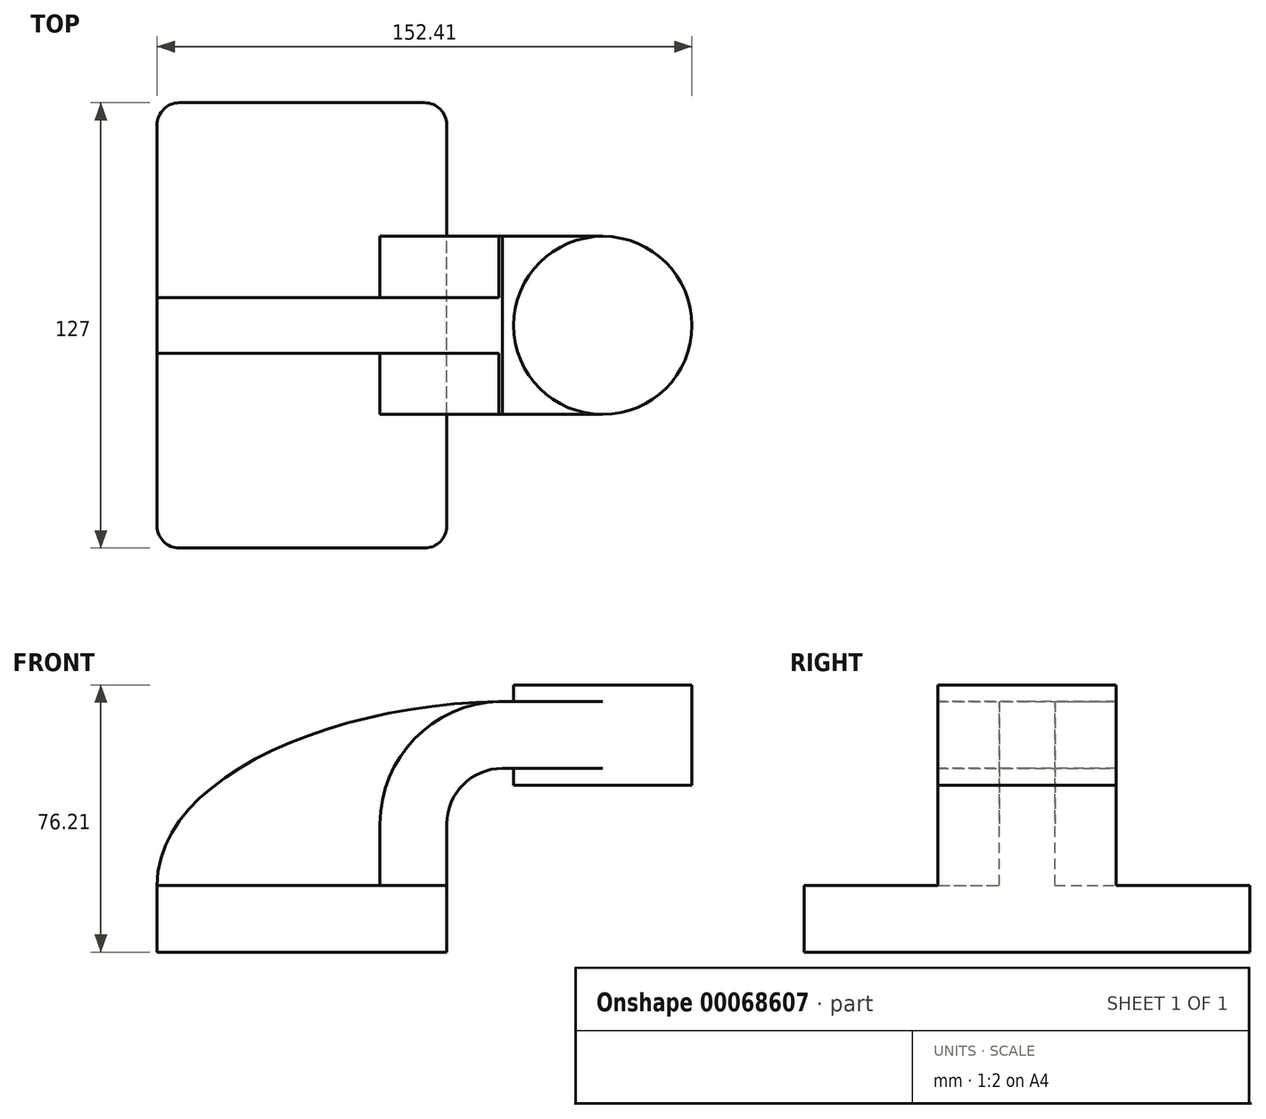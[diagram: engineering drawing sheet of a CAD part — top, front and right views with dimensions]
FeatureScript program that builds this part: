
annotation { "Feature Type Name" : "Feature", "Feature Type Description" : "" }
export const myFeature = defineFeature(function(context is Context, id is Id, definition is map)
    precondition{}
    {
        {
            var Q0;
            Q0=qCreatedBy(makeId("Front.planeOp"),FACE);
            var sketch = newSketch(context, id + "F0", { "sketchPlane" : qUnion([Q0])});
            skLineSegment(sketch, "E0.rect.bottom", {"start": v(-41.28, 9.52) * mm, "end": v(41.27, 9.53) * mm});
            skLineSegment(sketch, "E0.rect.top", {"start": v(-41.28, -9.52) * mm, "end": v(41.28, -9.52) * mm});
            skLineSegment(sketch, "E0.rect.left", {"start": v(-41.28, 9.52) * mm, "end": v(-41.28, -9.53) * mm});
            skLineSegment(sketch, "E0.rect.right", {"start": v(41.27, 9.53) * mm, "end": v(41.28, -9.52) * mm});
            skPoint(sketch, "E0.rect.middle", {"position": v(0, 0) * mm});
            skLineSegment(sketch, "E1.rect.bottom", {"start": v(111.12, 38.1) * mm, "end": v(60.32, 38.1) * mm});
            skLineSegment(sketch, "E1.rect.top", {"start": v(111.12, 66.68) * mm, "end": v(60.32, 66.68) * mm});
            skLineSegment(sketch, "E1.rect.left", {"start": v(111.12, 38.1) * mm, "end": v(111.12, 66.68) * mm});
            skLineSegment(sketch, "E1.rect.right", {"start": v(60.32, 38.1) * mm, "end": v(60.32, 66.68) * mm});
            skPoint(sketch, "E1.rect.middle", {"position": v(85.72, 52.39) * mm});
            skLineSegment(sketch, "E2", {"start": v(41.27, 9.53) * mm, "end": v(41.27, 27) * mm});
            skArc(sketch, "E3", {"start": v(41.27, 27) * mm, "mid": v(45.92, 38.23) * mm, "end": v(57.15, 42.88) * mm});
            skLineSegment(sketch, "E4", {"start": v(57.15, 42.88) * mm, "end": v(85.72, 42.88) * mm});
            skLineSegment(sketch, "E5.0", {"start": v(57.15, 61.93) * mm, "end": v(85.72, 61.93) * mm});
            skArc(sketch, "E5.1", {"start": v(22.22, 27) * mm, "mid": v(32.45, 51.7) * mm, "end": v(57.15, 61.93) * mm});
            skLineSegment(sketch, "E5.2", {"start": v(22.22, 9.53) * mm, "end": v(22.22, 27) * mm});
            skLineSegment(sketch, "E6", {"start": v(85.72, 38.1) * mm, "end": v(85.72, 66.68) * mm});
            skFitSpline(sketch, "E7", {"points": [v(-41.28, 9.52) * mm, v(57.15, 61.93) * mm], "startDerivative": vector(-0.17, 91.25) * mm, "endDerivative": vector(148.08, 1.73) * mm});
            skPoint(sketch, "E8.1.internal.snap0", {"position": v(32.45, 51.7) * mm});
            skSolve(sketch);
        }
        {
            var Q0;
            Q0=makeQuery(id+"F0.imprint","IMPRINT",FACE,{"disambiguationData":[TD([[makeQuery(id+"F0.imprint","IMPRINT",EDGE,{"derivedFrom":sQuery(id+"F0.wireOp",EDGE,"E0.rect.top")}),1.0]])]});
            extrude(context, id + "F1", {"entities" : qUnion([Q0]), "endBound" : BoundingType.SYMMETRIC, "depth" : 127 * mm});
        }
        {
            var Q0;
            {var subQ1=sQuery(id+"F0.wireOp",EDGE,"E2");Q0=makeQuery(id+"F0.imprint","IMPRINT",FACE,{"disambiguationData":[TD([[makeQuery(id+"F0.imprint","IMPRINT",EDGE,{"derivedFrom":subQ1}),1.0]])]});}
            var Q1;
            {var subQ0=sQuery(id+"F0.wireOp",EDGE,"E4");var subQ1=sQuery(id+"F0.wireOp",EDGE,"E1.rect.right");var subQ2=makeQuery(id+"F0.imprint","INTERSECT",VERTEX,{"derivedFrom":[subQ1,subQ0]});Q1=makeQuery(id+"F0.imprint","IMPRINT",FACE,{"disambiguationData":[TD([[makeQuery(id+"F0.imprint","IMPRINT",EDGE,{"disambiguationData":[TD([[subQ2,-1.0]])],"derivedFrom":subQ1}),-1.0]])]});}
            extrude(context, id + "F2", {"entities" : qUnion([Q0, Q1]), "operationType" : NewBodyOperationType.ADD, "endBound" : BoundingType.SYMMETRIC, "depth" : 50.8 * mm});
        }
        {
            var Q0;
            {var subQ3=sQuery(id+"F0.wireOp",EDGE,"E5.2");Q0=makeQuery(id+"F0.imprint","IMPRINT",FACE,{"disambiguationData":[TD([[makeQuery(id+"F0.imprint","IMPRINT",EDGE,{"derivedFrom":subQ3}),1.0]])]});}
            extrude(context, id + "F3", {"entities" : qUnion([Q0]), "operationType" : NewBodyOperationType.ADD, "endBound" : BoundingType.SYMMETRIC, "depth" : 15.88 * mm});
        }
        {
            var Q0;
            {var subQ0=sQuery(id+"F0.wireOp",EDGE,"E1.rect.left");Q0=makeQuery(id+"F0.imprint","IMPRINT",FACE,{"disambiguationData":[TD([[makeQuery(id+"F0.imprint","IMPRINT",EDGE,{"derivedFrom":subQ0}),1.0]])]});}
            var Q1;
            Q1=sQuery(id+"F0.wireOp",EDGE,"E6");
            revolve(context, id + "F4", {"operationType" : NewBodyOperationType.ADD, "entities" : qUnion([Q0]), "axis" : qUnion([Q1]), "revolveType" : RevolveType.FULL});
        }
        {
            var Q0;
            Q0=makeQuery(id+"F1.opExtrude","CAP_EDGE",EDGE,{"disambiguationData":[OSD([sQuery(id+"F0.wireOp",EDGE,"E0.rect.left")])],"isStart":false});
            var Q1;
            Q1=makeQuery(id+"F1.opExtrude","CAP_EDGE",EDGE,{"disambiguationData":[OSD([sQuery(id+"F0.wireOp",EDGE,"E0.rect.right")])],"isStart":false});
            var Q2;
            Q2=makeQuery(id+"F1.opExtrude","CAP_EDGE",EDGE,{"disambiguationData":[OSD([sQuery(id+"F0.wireOp",EDGE,"E0.rect.right")])],"isStart":true});
            var Q3;
            Q3=makeQuery(id+"F1.opExtrude","CAP_EDGE",EDGE,{"disambiguationData":[OSD([sQuery(id+"F0.wireOp",EDGE,"E0.rect.left")])],"isStart":true});
            fillet(context, id + "F5", {"entities" : qUnion([Q0, Q1, Q2, Q3]), "radius" : 6.35 * mm, "tangentPropagation" : true, "allowEdgeOverflow" : false});
        }
    });
